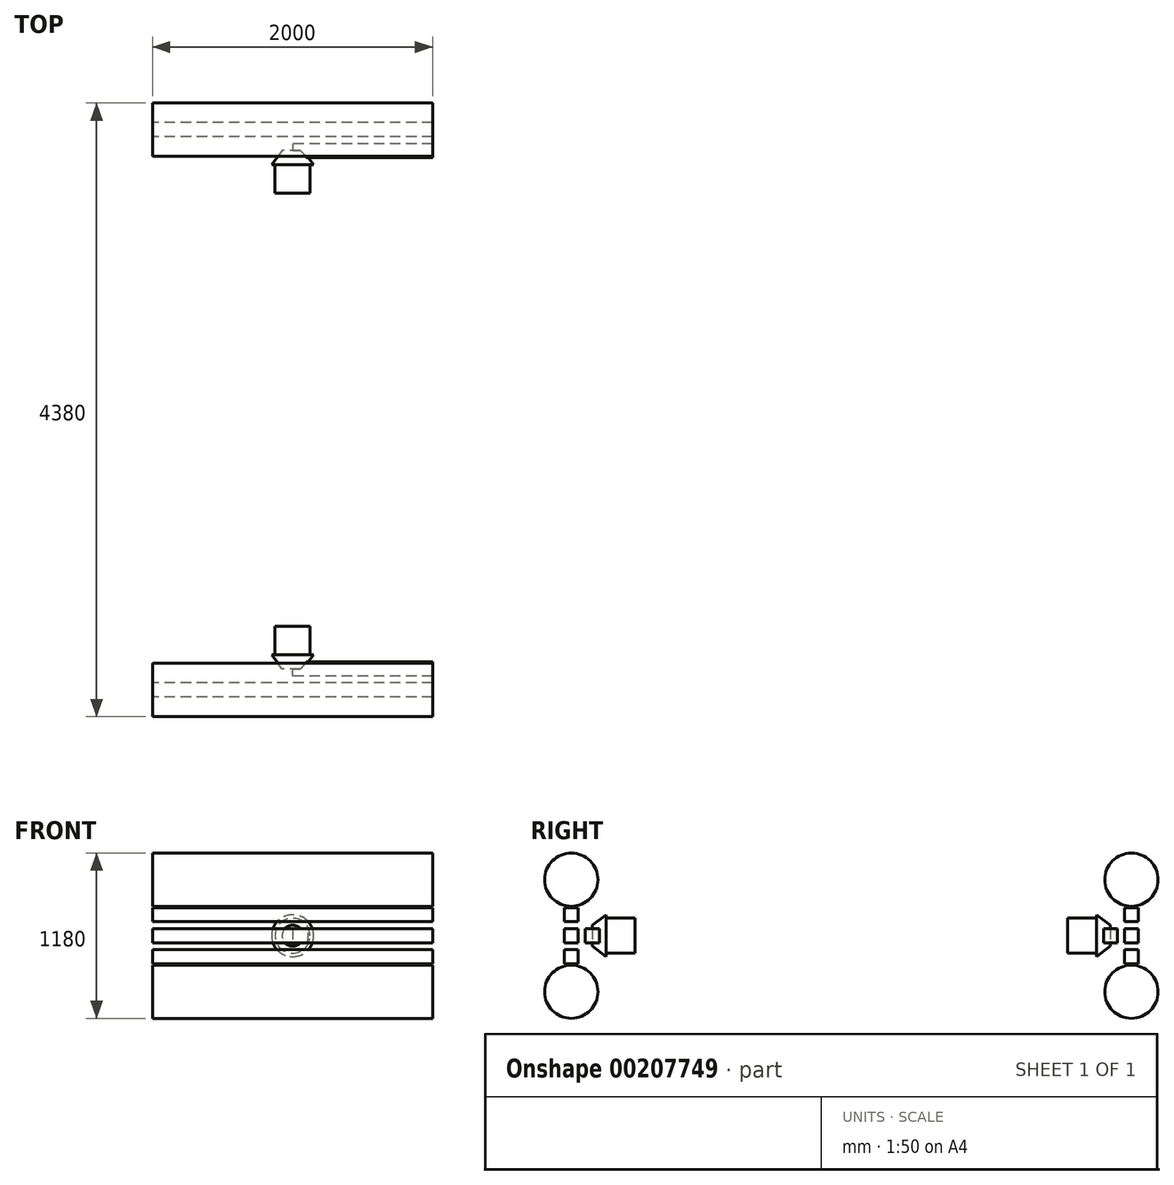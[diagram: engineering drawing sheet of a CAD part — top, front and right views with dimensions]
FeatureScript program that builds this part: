
annotation { "Feature Type Name" : "Feature", "Feature Type Description" : "" }
export const myFeature = defineFeature(function(context is Context, id is Id, definition is map)
    precondition{}
    {
        {
            var Q0;
            Q0=qCreatedBy(makeId("Right.planeOp"),FACE);
            var sketch = newSketch(context, id + "F0", { "sketchPlane" : qUnion([Q0])});
            skLineSegment(sketch, "E0.bottom", {"start": v(-1950, 950) * mm, "end": v(-2050, 950) * mm});
            skLineSegment(sketch, "E0.top", {"start": v(-1950, 850) * mm, "end": v(-2050, 850) * mm});
            skLineSegment(sketch, "E0.left", {"start": v(-1950, 950) * mm, "end": v(-1950, 850) * mm});
            skLineSegment(sketch, "E0.right", {"start": v(-2050, 950) * mm, "end": v(-2050, 850) * mm});
            skLineSegment(sketch, "E1.bottom", {"start": v(-1950, 800) * mm, "end": v(-2050, 800) * mm});
            skLineSegment(sketch, "E1.top", {"start": v(-1950, 700) * mm, "end": v(-2050, 700) * mm});
            skLineSegment(sketch, "E1.left", {"start": v(-1950, 800) * mm, "end": v(-1950, 700) * mm});
            skLineSegment(sketch, "E1.right", {"start": v(-2050, 800) * mm, "end": v(-2050, 700) * mm});
            skLineSegment(sketch, "E2.bottom", {"start": v(-1950, 1100) * mm, "end": v(-2050, 1100) * mm});
            skLineSegment(sketch, "E2.top", {"start": v(-1950, 1000) * mm, "end": v(-2050, 1000) * mm});
            skLineSegment(sketch, "E2.left", {"start": v(-1950, 1100) * mm, "end": v(-1950, 1000) * mm});
            skLineSegment(sketch, "E2.right", {"start": v(-2050, 1100) * mm, "end": v(-2050, 1000) * mm});
            skCircle(sketch, "E3", {"center": v(-2000, 500) * mm, "radius": 190 * mm});
            skCircle(sketch, "E4", {"center": v(-2000, 1300) * mm, "radius": 190 * mm});
            skLineSegment(sketch, "E5", {"start": v(-2050, 900) * mm, "end": v(-1950, 900) * mm, "construction": true});
            skLineSegment(sketch, "E6", {"start": v(-1950, 1050) * mm, "end": v(-2050, 1050) * mm, "construction": true});
            skLineSegment(sketch, "E7", {"start": v(-1950, 750) * mm, "end": v(-2050, 750) * mm, "construction": true});
            skLineSegment(sketch, "E8", {"start": v(-2000, 950) * mm, "end": v(-2000, 850) * mm, "construction": true});
            skSolve(sketch);
        }
        {
            var Q0;
            Q0 = qSketchRegion(id + "F0", true);
            extrude(context, id + "F1", {"entities" : qUnion([Q0]), "endBound" : BoundingType.SYMMETRIC, "depth" : 2000 * mm, "offsetDistance" : 25 * mm});
        }
        {
            var Q0;
            Q0=qCreatedBy(makeId("Right.planeOp"),FACE);
            var sketch = newSketch(context, id + "F2", { "sketchPlane" : qUnion([Q0])});
            skLineSegment(sketch, "E9.bottom", {"start": v(-1900, 950) * mm, "end": v(-1800, 950) * mm});
            skLineSegment(sketch, "E9.top", {"start": v(-1900, 850) * mm, "end": v(-1800, 850) * mm});
            skLineSegment(sketch, "E9.left", {"start": v(-1900, 950) * mm, "end": v(-1900, 850) * mm});
            skLineSegment(sketch, "E9.right", {"start": v(-1800, 950) * mm, "end": v(-1800, 850) * mm});
            skSolve(sketch);
        }
        {
            var Q0;
            Q0=makeQuery(id+"F2.imprint","IMPRINT",FACE,{"disambiguationData":[TD([[makeQuery(id+"F2.imprint","IMPRINT",EDGE,{"derivedFrom":sQuery(id+"F2.wireOp",EDGE,"E9.bottom")}),-1.0]])]});
            var Q1;
            Q1=makeQuery(id+"F1.opExtrude","CAP_FACE",FACE,{"disambiguationData":[OSD([sQuery(id+"F0.wireOp",EDGE,"E0.bottom"),sQuery(id+"F0.wireOp",EDGE,"E0.top"),sQuery(id+"F0.wireOp",EDGE,"E0.left"),sQuery(id+"F0.wireOp",EDGE,"E0.right")])],"isStart":false});
            extrude(context, id + "F3", {"entities" : qUnion([Q0]), "endBound" : BoundingType.UP_TO_SURFACE, "depth" : 25 * mm, "endBoundEntityFace" : qUnion([Q1]), "offsetDistance" : 25 * mm});
        }
        {
            var Q0;
            Q0=qCreatedBy(makeId("Right.planeOp"),FACE);
            var sketch = newSketch(context, id + "F4", { "sketchPlane" : qUnion([Q0])});
            skLineSegment(sketch, "E10", {"start": v(-1900, 900) * mm, "end": v(-1800, 900) * mm, "construction": true});
            skLineSegment(sketch, "E11", {"start": v(-1850, 900) * mm, "end": v(-1850, 975) * mm});
            skLineSegment(sketch, "E12", {"start": v(-1850, 975) * mm, "end": v(-1750, 1050) * mm});
            skLineSegment(sketch, "E13", {"start": v(-1750, 1050) * mm, "end": v(-1750, 1025) * mm});
            skLineSegment(sketch, "E14", {"start": v(-1750, 1025) * mm, "end": v(-1545, 1025) * mm});
            skLineSegment(sketch, "E15", {"start": v(-1545, 1025) * mm, "end": v(-1545, 900) * mm});
            skLineSegment(sketch, "E16", {"start": v(-1545, 900) * mm, "end": v(-1850, 900) * mm});
            skSolve(sketch);
        }
        {
            var Q0;
            Q0 = qSketchRegion(id + "F4", true);
            var Q1;
            Q1=sQuery(id+"F4.wireOp",EDGE,"E10");
            revolve(context, id + "F5", {"operationType" : NewBodyOperationType.ADD, "surfaceOperationType" : NewSurfaceOperationType.NEW, "entities" : qUnion([Q0]), "axis" : qUnion([Q1]), "revolveType" : RevolveType.FULL});
        }
        {
            var Q0;
            Q0=makeQuery(id+"F3.opExtrude","SWEPT_BODY",BODY,{"disambiguationData":[OSD([sQuery(id+"F2.wireOp",EDGE,"E9.bottom"),sQuery(id+"F2.wireOp",EDGE,"E9.top"),sQuery(id+"F2.wireOp",EDGE,"E9.left"),sQuery(id+"F2.wireOp",EDGE,"E9.right")])]});
            var Q1;
            Q1=makeQuery(id+"F1.opExtrude","SWEPT_BODY",BODY,{"disambiguationData":[OSD([sQuery(id+"F0.wireOp",EDGE,"E2.bottom"),sQuery(id+"F0.wireOp",EDGE,"E2.top"),sQuery(id+"F0.wireOp",EDGE,"E2.left"),sQuery(id+"F0.wireOp",EDGE,"E2.right")])]});
            var Q2;
            Q2=makeQuery(id+"F1.opExtrude","SWEPT_BODY",BODY,{"disambiguationData":[OSD([sQuery(id+"F0.wireOp",EDGE,"E0.bottom"),sQuery(id+"F0.wireOp",EDGE,"E0.top"),sQuery(id+"F0.wireOp",EDGE,"E0.left"),sQuery(id+"F0.wireOp",EDGE,"E0.right")])]});
            var Q3;
            Q3=makeQuery(id+"F1.opExtrude","SWEPT_BODY",BODY,{"disambiguationData":[OSD([sQuery(id+"F0.wireOp",EDGE,"E1.bottom"),sQuery(id+"F0.wireOp",EDGE,"E1.top"),sQuery(id+"F0.wireOp",EDGE,"E1.left"),sQuery(id+"F0.wireOp",EDGE,"E1.right")])]});
            var Q4;
            Q4=makeQuery(id+"F1.opExtrude","SWEPT_BODY",BODY,{"disambiguationData":[OSD([sQuery(id+"F0.wireOp",EDGE,"E4")])]});
            var Q5;
            Q5=makeQuery(id+"F1.opExtrude","SWEPT_BODY",BODY,{"disambiguationData":[OSD([sQuery(id+"F0.wireOp",EDGE,"E3")])]});
            var Q6;
            Q6=qCreatedBy(makeId("Front.planeOp"),FACE);
            mirror(context, id + "F6", {"entities" : qUnion([Q0, Q1, Q2, Q3, Q4, Q5]), "mirrorPlane" : qUnion([Q6])});
        }
    });
